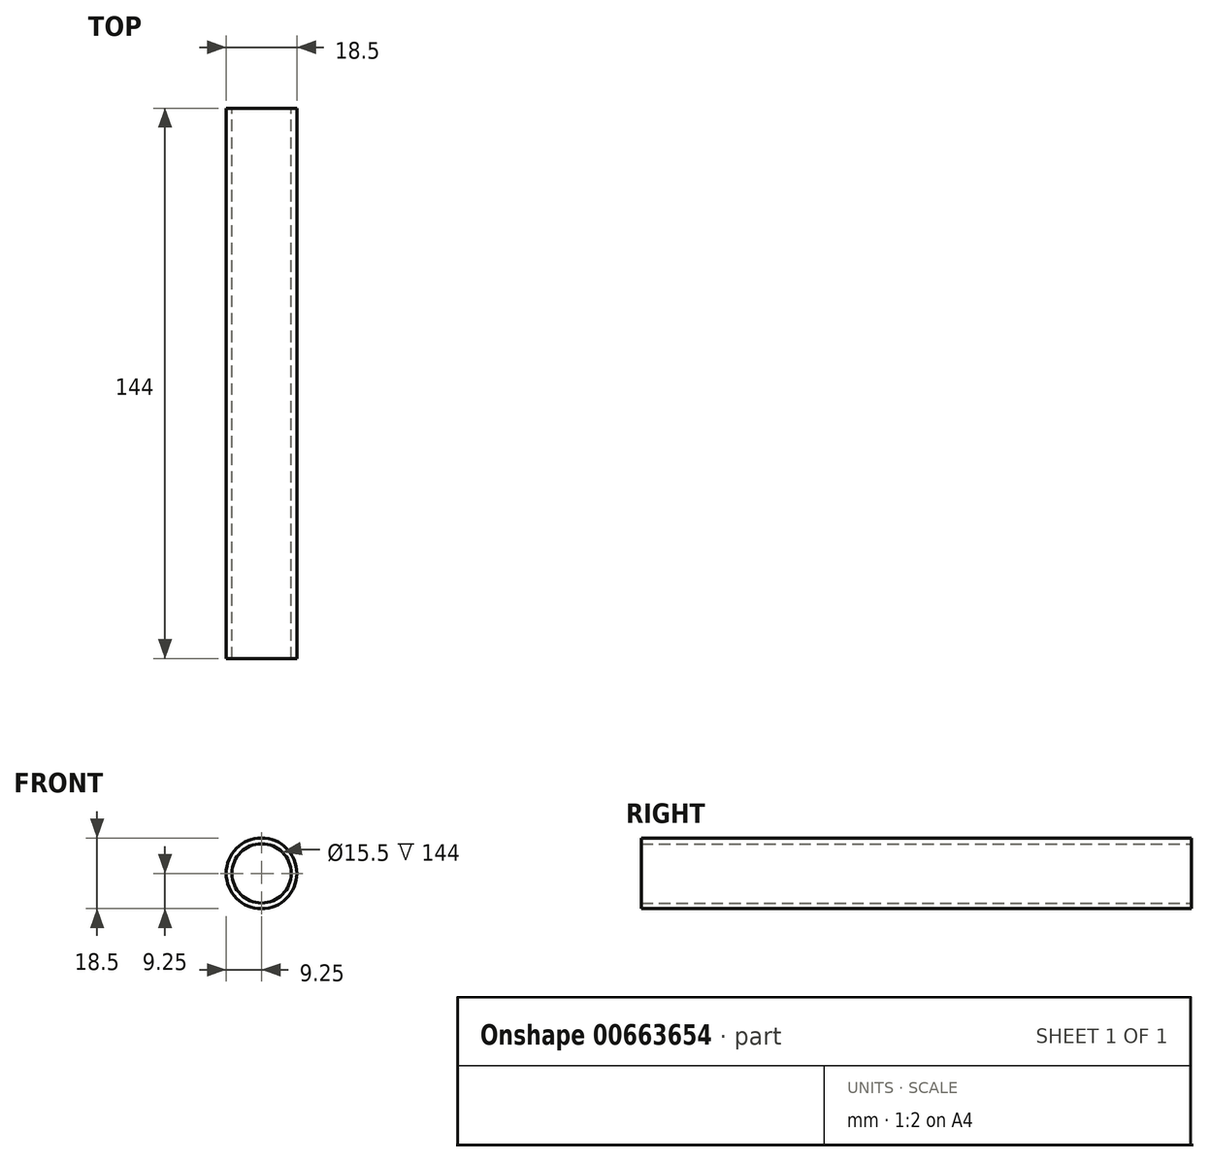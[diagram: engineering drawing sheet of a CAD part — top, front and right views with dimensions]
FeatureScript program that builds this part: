
annotation { "Feature Type Name" : "Feature", "Feature Type Description" : "" }
export const myFeature = defineFeature(function(context is Context, id is Id, definition is map)
    precondition{}
    {
        {
            var Q0;
            Q0=qCreatedBy(makeId("Front.planeOp"),FACE);
            var sketch = newSketch(context, id + "F0", { "sketchPlane" : qUnion([Q0])});
            skCircle(sketch, "E0", {"center": v(0, 0) * mm, "radius": 9.25 * mm});
            skCircle(sketch, "E1.0", {"center": v(0, 0) * mm, "radius": 7.75 * mm});
            skSolve(sketch);
        }
        {
            var Q0;
            Q0=qSketchRegion(id+"F0",true);
            extrude(context, id + "F1", {"entities" : qUnion([Q0]), "depth" : 144 * mm, "offsetDistance" : 25 * mm});
        }
    });
